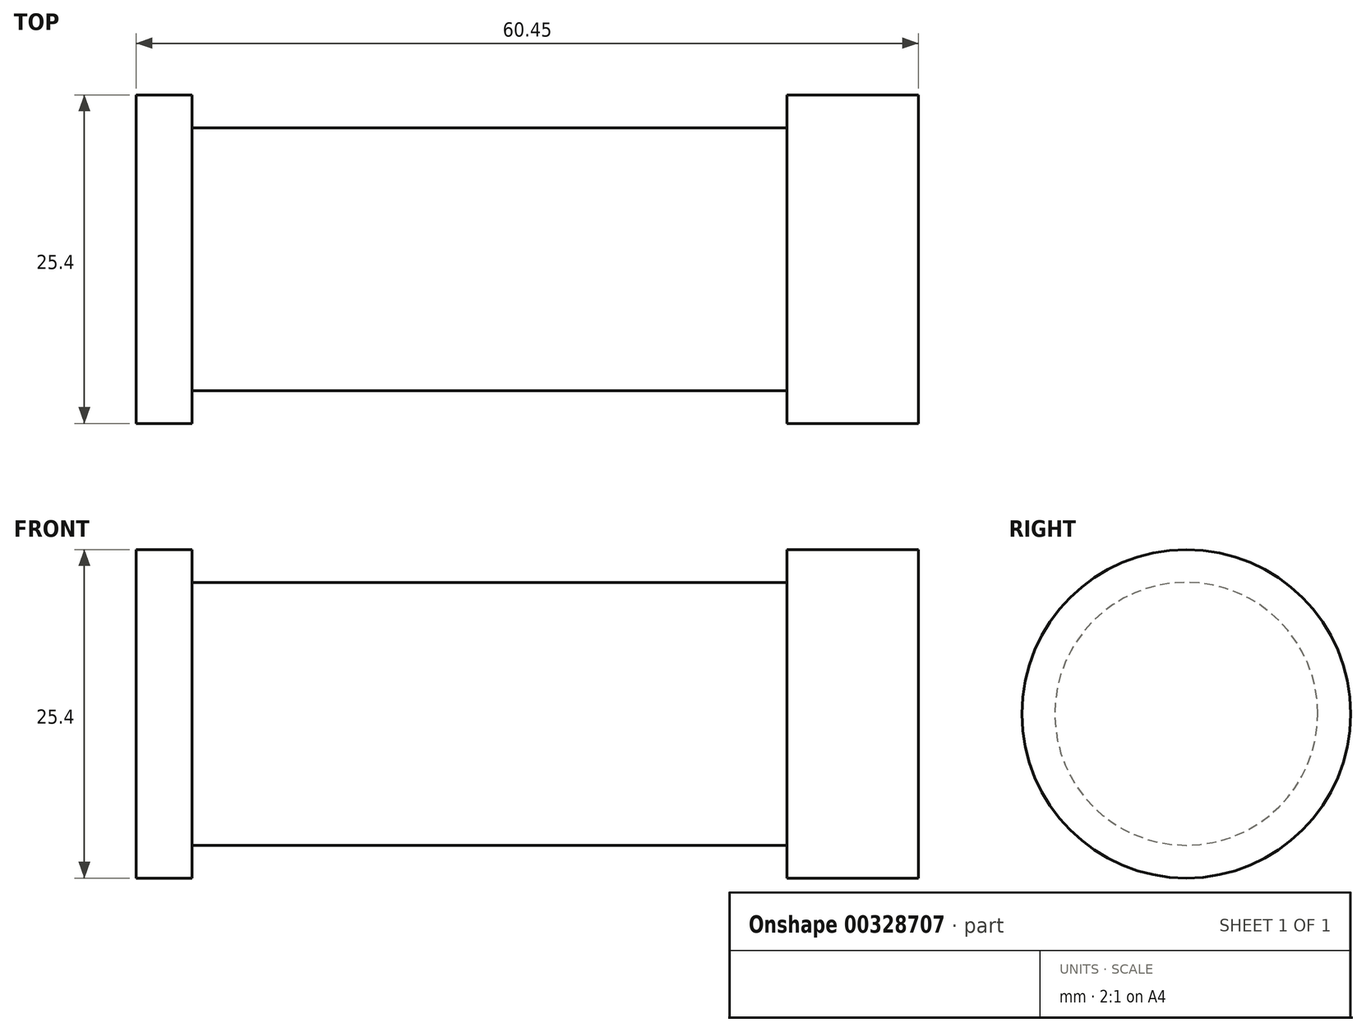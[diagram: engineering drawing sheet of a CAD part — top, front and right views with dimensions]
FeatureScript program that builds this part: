
annotation { "Feature Type Name" : "Feature", "Feature Type Description" : "" }
export const myFeature = defineFeature(function(context is Context, id is Id, definition is map)
    precondition{}
    {
        {
            var Q0;
            Q0=qCreatedBy(makeId("Front.planeOp"),FACE);
            var sketch = newSketch(context, id + "F0", { "sketchPlane" : qUnion([Q0])});
            skLineSegment(sketch, "E0", {"start": v(0, 0) * mm, "end": v(0, 12.7) * mm});
            skLineSegment(sketch, "E1", {"start": v(0, 12.7) * mm, "end": v(10.16, 12.7) * mm});
            skLineSegment(sketch, "E2", {"start": v(10.16, 12.7) * mm, "end": v(10.16, 10.16) * mm});
            skLineSegment(sketch, "E3", {"start": v(10.16, 10.16) * mm, "end": v(56.13, 10.16) * mm});
            skLineSegment(sketch, "E4", {"start": v(56.13, 10.16) * mm, "end": v(56.13, 12.7) * mm});
            skLineSegment(sketch, "E5", {"start": v(56.13, 12.7) * mm, "end": v(66.3, 12.7) * mm});
            skLineSegment(sketch, "E6", {"start": v(66.3, 12.7) * mm, "end": v(66.3, 0) * mm});
            skLineSegment(sketch, "E7", {"start": v(66.3, 0) * mm, "end": v(0, 0) * mm});
            skLineSegment(sketch, "E8", {"start": v(5.84, 15.24) * mm, "end": v(-0.5, 15.24) * mm});
            skLineSegment(sketch, "E9", {"start": v(-0.5, 15.24) * mm, "end": v(-10.88, 3.85) * mm});
            skLineSegment(sketch, "E10", {"start": v(0, 0) * mm, "end": v(-6.65, 0) * mm});
            skCircle(sketch, "E11", {"center": v(-6.65, 0) * mm, "radius": 5.72 * mm});
            skCircle(sketch, "E12", {"center": v(-6.65, 0) * mm, "radius": 3.18 * mm});
            skLineSegment(sketch, "E13", {"start": v(5.84, 15.24) * mm, "end": v(5.84, -9.4) * mm});
            skLineSegment(sketch, "E14", {"start": v(5.84, -9.4) * mm, "end": v(-8.18, -5.5) * mm});
            skSolve(sketch);
        }
        {
            var Q0;
            {var subQ0=sQuery(id+"F0.wireOp",EDGE,"E2");Q0=makeQuery(id+"F0.imprint","IMPRINT",FACE,{"disambiguationData":[TD([[makeQuery(id+"F0.imprint","IMPRINT",EDGE,{"derivedFrom":subQ0}),-1.0]])]});}
            var Q1;
            Q1=sQuery(id+"F0.wireOp",EDGE,"E7");
            revolve(context, id + "F1", {"entities" : qUnion([Q0]), "axis" : qUnion([Q1]), "revolveType" : RevolveType.FULL});
        }
    });
